# Revit family: Shower_Hand_Caroma_Liano Nexus Multi Function
name_source: partatom
category: Plumbing Fixtures
revit_build: Autodesk Revit MEP 2014 (Build: 20140709_2115(x64)
units: mm (PartAtom-declared; Revit-internal decimal feet)

## types (1)
- Standard
    Assembly Code = D2010710
    CW Connection = Yes
    ConnectorDiameter = 20 mm  [stored 0.0656168 ft]
    Cost = 0 $
    Default Elevation = 1650 mm  [stored 5.41339 ft]
    Description = TBC
    HW Connection = Yes
    Manufacturer = Caroma
    Material_ANZRS = Metal-Chrome-Caroma
    Model = 91059C3A
    ModifiedIssue_ANZRS = 20160204.54 $
    Type Comments = Caroma Liano Nexus Multi Function Hand Shower
    URL = http://specify.caroma.com.au
    Vent Connection = No
    WELSRating_ANZRS = WELS 3 star rated, 9L/min
    Waste Connection = No

note: [stored X ft] marks values corroborated as IEEE doubles in the binary element streams (Revit-internal decimal feet)

## geometry (parser evidence)
native form markers: Revolve x1, Sweep x2
no freeform markers — native parametric forms only
